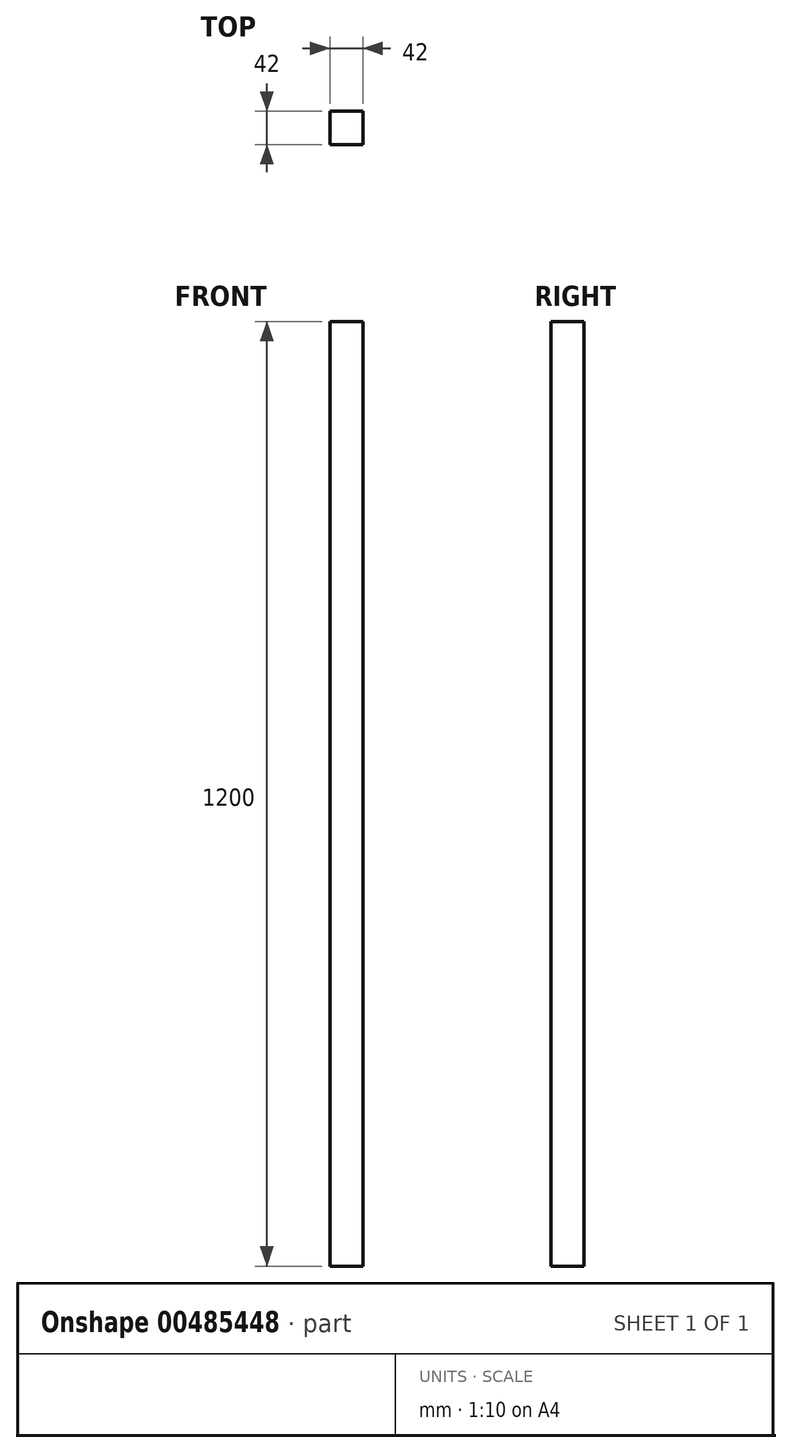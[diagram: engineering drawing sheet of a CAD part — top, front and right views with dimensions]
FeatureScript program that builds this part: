
annotation { "Feature Type Name" : "Feature", "Feature Type Description" : "" }
export const myFeature = defineFeature(function(context is Context, id is Id, definition is map)
    precondition{}
    {
        {
            var Q0;
            Q0=qCreatedBy(makeId("Top.planeOp"),FACE);
            var sketch = newSketch(context, id + "F0", { "sketchPlane" : qUnion([Q0])});
            skLineSegment(sketch, "E0.bottom", {"start": v(21, 21) * mm, "end": v(-21, 21) * mm});
            skLineSegment(sketch, "E0.top", {"start": v(21, -21) * mm, "end": v(-21, -21) * mm});
            skLineSegment(sketch, "E0.left", {"start": v(21, 21) * mm, "end": v(21, -21) * mm});
            skLineSegment(sketch, "E0.right", {"start": v(-21, 21) * mm, "end": v(-21, -21) * mm});
            skPoint(sketch, "E0.middle", {"position": v(0, 0) * mm});
            skSolve(sketch);
        }
        {
            var Q0;
            Q0=makeQuery(id+"F0.imprint","IMPRINT",FACE,{"disambiguationData":[TD([[makeQuery(id+"F0.imprint","IMPRINT",EDGE,{"derivedFrom":sQuery(id+"F0.wireOp",EDGE,"E0.bottom")}),1.0]])]});
            extrude(context, id + "F1", {"entities" : qUnion([Q0]), "depth" : 1200 * mm});
        }
    });
